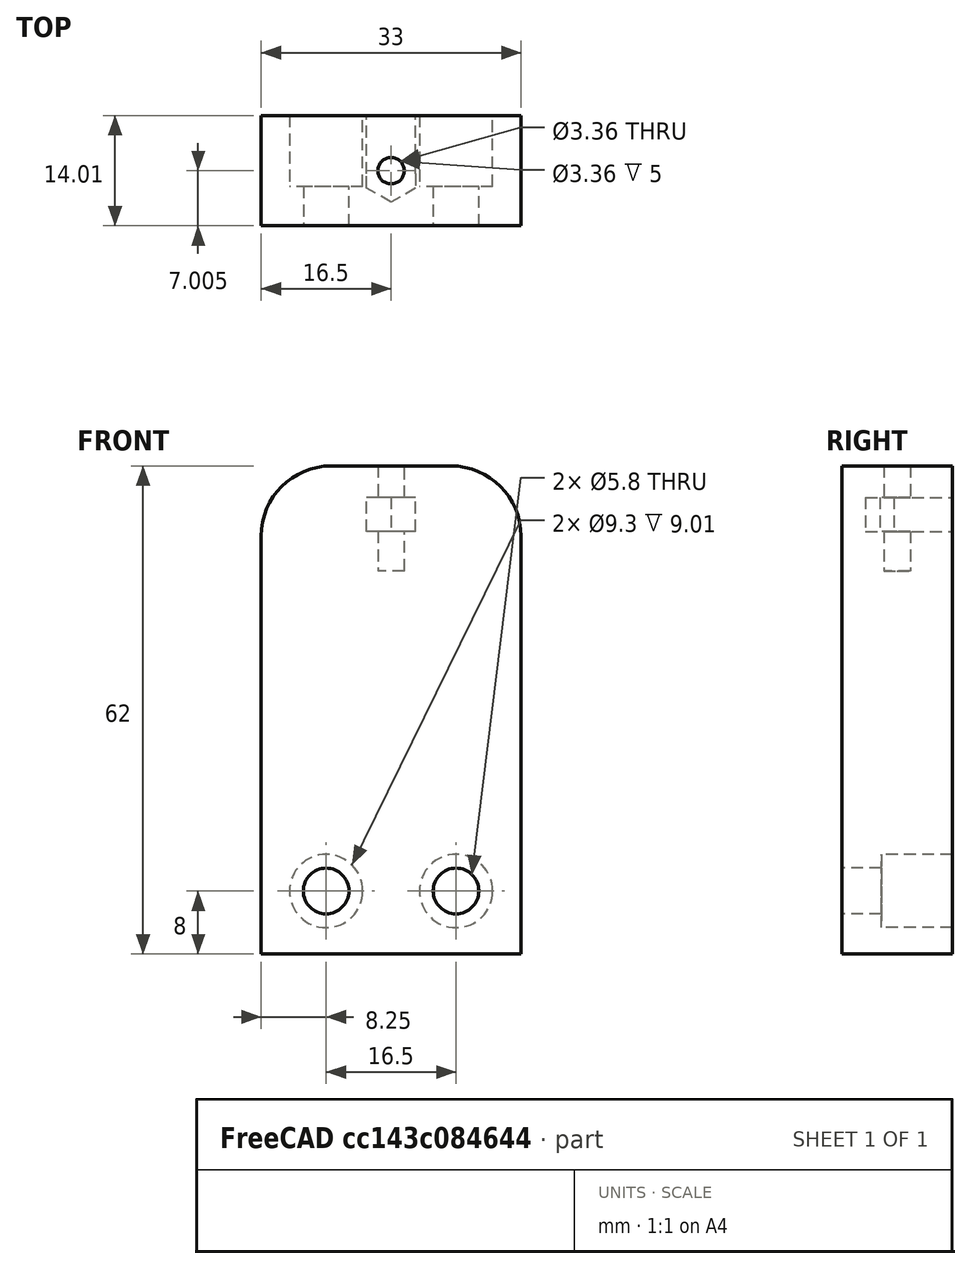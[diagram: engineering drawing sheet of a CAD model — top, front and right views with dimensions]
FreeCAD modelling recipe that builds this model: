
FCSTD DOCUMENT  (FreeCAD 0.16R6706 (Git))
Label: idler_pulley_holder_44_above_h
License: All rights reserved
LicenseURL: http://en.wikipedia.org/wiki/All_rights_reserved
objects: Part::Feature×1, Part::Fillet×1, Part::Prism×1, Part::Box×1, Part::Fuse×1, Part::Cut×1
note: 6 computed .brp shape members not serialized (recipe doc carries the construction recipe); baked Part::Feature solids carry a one-line shape summary decoded from their .brp

FEATURE [Part::Feature] idlepulleyhold_aux
  shape: bbox 33 x 14.01 x 62 mm, 14 faces (baked)
FEATURE [Part::Fillet] idlepulleyhold_chmf
  Base = -> idlepulleyhold_aux
  Edges = 2 edges r=8.895: [Edge9,Edge12]
FEATURE [Part::Prism] idlepulleyhold_nuthole_nut
  Circumradius = 3.605
  Height = 4.32
  Placement = pos=(0,0,0) rot=(-0.57735,0.57735,0.57735;2.0944rad)
  Polygon = 6
FEATURE [Part::Box] idlepulleyhold_nuthole_hole
  Height = 8.405
  Length = 6.24408
  Placement = pos=(-3.12204,0,0) rot=(0,0,1;0rad)
  Width = 4.32
FEATURE [Part::Fuse] idlepulleyhold_nuthole
  Base = -> idlepulleyhold_nuthole_nut
  Placement = pos=(0,6.605,40) rot=(-1,0,0;1.5708rad)
  Tool = -> idlepulleyhold_nuthole_hole
FEATURE [Part::Cut] idlepulleyhold
  Base = -> idlepulleyhold_chmf
  Tool = -> idlepulleyhold_nuthole
